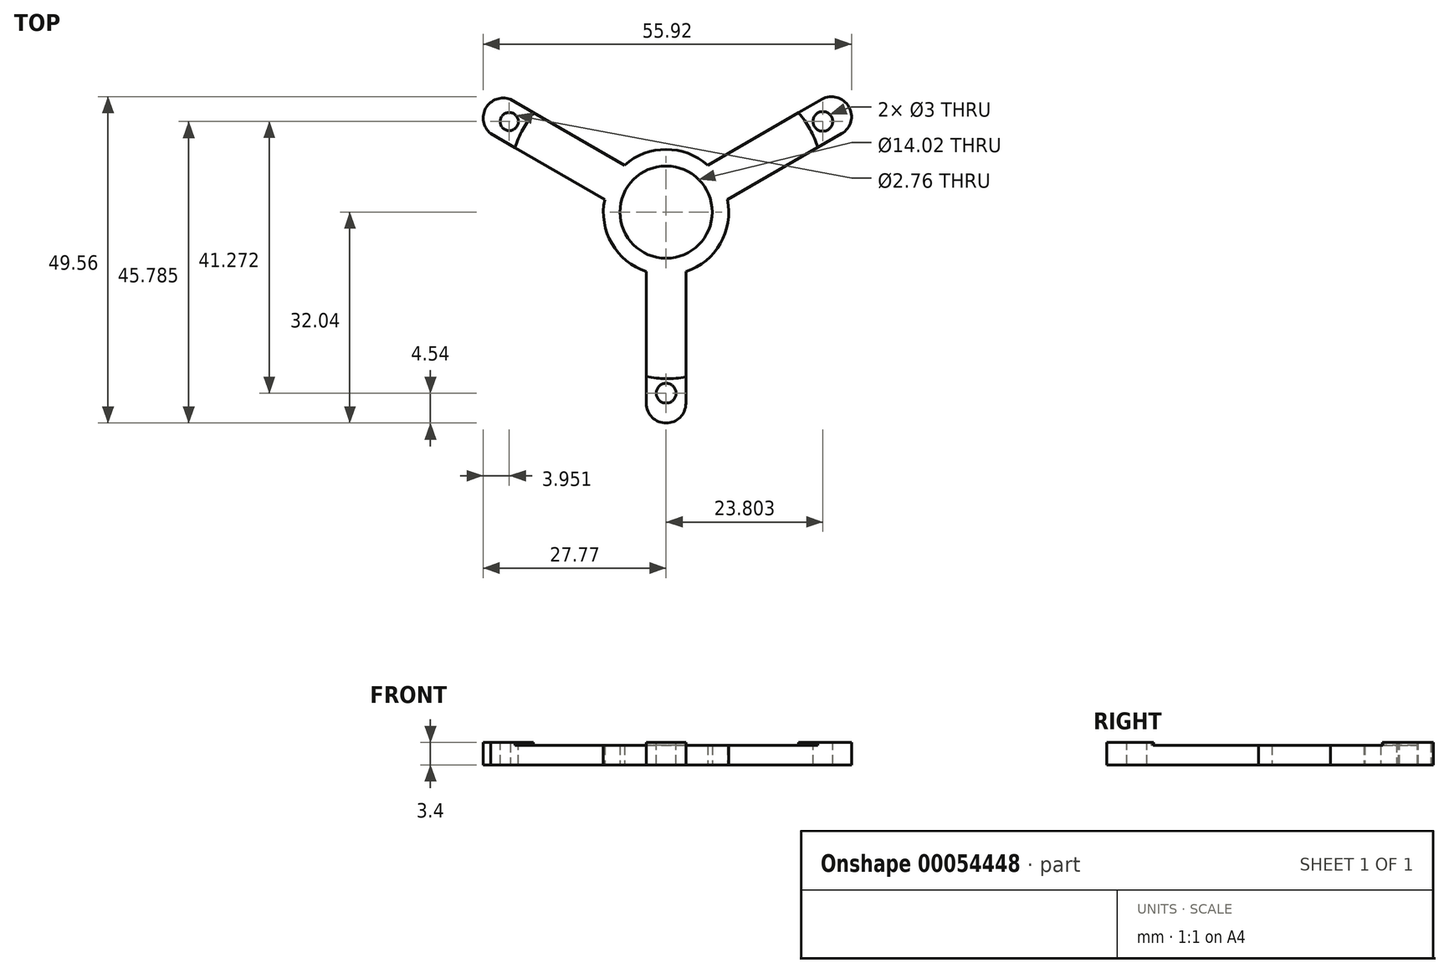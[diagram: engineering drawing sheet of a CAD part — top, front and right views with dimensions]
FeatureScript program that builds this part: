
annotation { "Feature Type Name" : "Feature", "Feature Type Description" : "" }
export const myFeature = defineFeature(function(context is Context, id is Id, definition is map)
    precondition{}
    {
        {
            var Q0;
            Q0=qCreatedBy(makeId("Top.planeOp"),FACE);
            var sketch = newSketch(context, id + "F0", { "sketchPlane" : qUnion([Q0])});
            skCircle(sketch, "E0", {"center": v(0, 0) * mm, "radius": 25.15 * mm, "construction": true});
            skCircle(sketch, "E1", {"center": v(0, 0) * mm, "radius": 30 * mm, "construction": true});
            skLineSegment(sketch, "E2", {"start": v(0, 0) * mm, "end": v(0, -27.5) * mm, "construction": true});
            skLineSegment(sketch, "E3", {"start": v(0, 0) * mm, "end": v(-23.82, 13.75) * mm, "construction": true});
            skLineSegment(sketch, "E4", {"start": v(0, 0) * mm, "end": v(23.82, 13.75) * mm, "construction": true});
            skCircle(sketch, "E5", {"center": v(0, 0) * mm, "radius": 7 * mm, "construction": true});
            skSolve(sketch);
        }
        {
            var Q0;
            Q0=qCreatedBy(makeId("Top.planeOp"),FACE);
            var sketch = newSketch(context, id + "F1", { "sketchPlane" : qUnion([Q0])});
            skCircle(sketch, "E6", {"center": v(0, 0) * mm, "radius": 7 * mm});
            skCircle(sketch, "E7", {"center": v(0, 0) * mm, "radius": 9.52 * mm});
            skLineSegment(sketch, "E8", {"start": v(-6.33, 7.12) * mm, "end": v(-23.65, 17.12) * mm});
            skLineSegment(sketch, "E9", {"start": v(-9.33, 1.92) * mm, "end": v(-26.65, 11.92) * mm});
            skArc(sketch, "E10", {"start": v(-23.65, 17.12) * mm, "mid": v(-27.37, 15.8) * mm, "end": v(-26.65, 11.92) * mm});
            skLineSegment(sketch, "E11", {"start": v(6.33, 7.12) * mm, "end": v(23.65, 17.12) * mm});
            skLineSegment(sketch, "E12", {"start": v(9.33, 1.92) * mm, "end": v(26.65, 11.92) * mm});
            skArc(sketch, "E13", {"start": v(26.65, 11.92) * mm, "mid": v(27.74, 16.02) * mm, "end": v(23.65, 17.12) * mm});
            skLineSegment(sketch, "E14", {"start": v(-3, -9.04) * mm, "end": v(-3, -29.04) * mm});
            skLineSegment(sketch, "E15", {"start": v(3, -9.04) * mm, "end": v(3, -29.04) * mm});
            skArc(sketch, "E16", {"start": v(-3, -29.04) * mm, "mid": v(0, -32.04) * mm, "end": v(3, -29.04) * mm});
            skSolve(sketch);
        }
        {
            var Q0;
            {var subQ0=sQuery(id+"F1.wireOp",EDGE,"E11");Q0=makeQuery(id+"F1.imprint","IMPRINT",FACE,{"disambiguationData":[TD([[makeQuery(id+"F1.imprint","IMPRINT",EDGE,{"derivedFrom":subQ0}),-1.0]])]});}
            var Q1;
            {var subQ0=sQuery(id+"F1.wireOp",EDGE,"E14");Q1=makeQuery(id+"F1.imprint","IMPRINT",FACE,{"disambiguationData":[TD([[makeQuery(id+"F1.imprint","IMPRINT",EDGE,{"derivedFrom":subQ0}),1.0]])]});}
            var Q2;
            Q2=makeQuery(id+"F1.imprint","IMPRINT",FACE,{"disambiguationData":[TD([[makeQuery(id+"F1.imprint","IMPRINT",EDGE,{"derivedFrom":sQuery(id+"F1.wireOp",EDGE,"E6")}),-1.0]])]});
            var Q3;
            {var subQ0=sQuery(id+"F1.wireOp",EDGE,"E8");Q3=makeQuery(id+"F1.imprint","IMPRINT",FACE,{"disambiguationData":[TD([[makeQuery(id+"F1.imprint","IMPRINT",EDGE,{"derivedFrom":subQ0}),1.0]])]});}
            extrude(context, id + "F2", {"entities" : qUnion([Q0, Q1, Q2, Q3]), "depth" : 3 * mm});
        }
        {
            var Q0;
            Q0=makeQuery(id+"F2.opExtrude","CAP_FACE",FACE,{"disambiguationData":[OSD([sQuery(id+"F1.wireOp",EDGE,"E6"),sQuery(id+"F1.wireOp",EDGE,"E7"),sQuery(id+"F1.wireOp",EDGE,"E8"),sQuery(id+"F1.wireOp",EDGE,"E9"),sQuery(id+"F1.wireOp",EDGE,"E10"),sQuery(id+"F1.wireOp",EDGE,"E11"),sQuery(id+"F1.wireOp",EDGE,"E12"),sQuery(id+"F1.wireOp",EDGE,"E13"),sQuery(id+"F1.wireOp",EDGE,"E14"),sQuery(id+"F1.wireOp",EDGE,"E15"),sQuery(id+"F1.wireOp",EDGE,"E16")])],"isStart":false});
            var sketch = newSketch(context, id + "F3", { "sketchPlane" : qUnion([Q0])});
            skCircle(sketch, "E17", {"center": v(-23.82, 13.75) * mm, "radius": 1.38 * mm});
            skCircle(sketch, "E18", {"center": v(23.8, 13.77) * mm, "radius": 1.5 * mm});
            skCircle(sketch, "E19", {"center": v(0, -40.74) * mm, "radius": 1.42 * mm});
            skCircle(sketch, "E20", {"center": v(0, -27.5) * mm, "radius": 1.5 * mm});
            skSolve(sketch);
        }
        {
            var Q0;
            Q0=makeQuery(id+"F3.imprint","IMPRINT",FACE,{"disambiguationData":[TD([[makeQuery(id+"F3.imprint","IMPRINT",EDGE,{"derivedFrom":sQuery(id+"F3.wireOp",EDGE,"E17")}),1.0]])]});
            var Q1;
            {var subQ0=sQuery(id+"F3.wireOp",EDGE,"E18");var subQ1=makeQuery(id+"F2.opExtrude","CAP_EDGE",EDGE,{"disambiguationData":[OSD([sQuery(id+"F1.wireOp",EDGE,"E11")])],"isStart":false});var subQ2=makeQuery(id+"F3.imprint","INTERSECT",VERTEX,{"disambiguationData":[OD(0.0)],"derivedFrom":[subQ1,subQ0]});Q1=makeQuery(id+"F3.imprint","IMPRINT",FACE,{"disambiguationData":[TD([[makeQuery(id+"F3.imprint","IMPRINT",EDGE,{"disambiguationData":[TD([[subQ2,-1.0]])],"derivedFrom":subQ0}),1.0]])]});}
            var Q2;
            {var subQ0=sQuery(id+"F3.wireOp",EDGE,"E20");var subQ1=makeQuery(id+"F3.imprint","INTERSECT",VERTEX,{"derivedFrom":[makeQuery(id+"F2.opExtrude","CAP_EDGE",EDGE,{"disambiguationData":[OSD([sQuery(id+"F1.wireOp",EDGE,"E14")])],"isStart":false}),subQ0]});Q2=makeQuery(id+"F3.imprint","IMPRINT",FACE,{"disambiguationData":[TD([[makeQuery(id+"F3.imprint","IMPRINT",EDGE,{"disambiguationData":[TD([[subQ1,1.0]])],"derivedFrom":subQ0}),1.0]])]});}
            extrude(context, id + "F4", {"entities" : qUnion([Q0, Q1, Q2]), "operationType" : NewBodyOperationType.REMOVE, "oppositeDirection" : true, "depth" : 25 * mm});
        }
        {
            var Q0;
            Q0=makeQuery(id+"F2.opExtrude","CAP_FACE",FACE,{"disambiguationData":[OSD([sQuery(id+"F1.wireOp",EDGE,"E6"),sQuery(id+"F1.wireOp",EDGE,"E7"),sQuery(id+"F1.wireOp",EDGE,"E8"),sQuery(id+"F1.wireOp",EDGE,"E9"),sQuery(id+"F1.wireOp",EDGE,"E10"),sQuery(id+"F1.wireOp",EDGE,"E11"),sQuery(id+"F1.wireOp",EDGE,"E12"),sQuery(id+"F1.wireOp",EDGE,"E13"),sQuery(id+"F1.wireOp",EDGE,"E14"),sQuery(id+"F1.wireOp",EDGE,"E15"),sQuery(id+"F1.wireOp",EDGE,"E16")])],"isStart":false});
            var sketch = newSketch(context, id + "F5", { "sketchPlane" : qUnion([Q0])});
            skArc(sketch, "E21", {"start": v(-20.13, 15.09) * mm, "mid": v(-21.76, 12.55) * mm, "end": v(-22.96, 9.8) * mm});
            skArc(sketch, "E22", {"start": v(23.04, 9.84) * mm, "mid": v(21.84, 12.6) * mm, "end": v(20.12, 15.08) * mm});
            skArc(sketch, "E23", {"start": v(-3, -24.94) * mm, "mid": v(0, -25.3) * mm, "end": v(3, -25.02) * mm});
            skSolve(sketch);
        }
        {
            var Q0;
            {var subQ2=sQuery(id+"F5.wireOp",EDGE,"E21");Q0=makeQuery(id+"F5.imprint","IMPRINT",FACE,{"disambiguationData":[TD([[makeQuery(id+"F5.imprint","IMPRINT",EDGE,{"derivedFrom":subQ2}),-1.0]])]});}
            var Q1;
            {var subQ2=sQuery(id+"F5.wireOp",EDGE,"E22");Q1=makeQuery(id+"F5.imprint","IMPRINT",FACE,{"disambiguationData":[TD([[makeQuery(id+"F5.imprint","IMPRINT",EDGE,{"derivedFrom":subQ2}),-1.0]])]});}
            var Q2;
            {var subQ2=sQuery(id+"F5.wireOp",EDGE,"E23");Q2=makeQuery(id+"F5.imprint","IMPRINT",FACE,{"disambiguationData":[TD([[makeQuery(id+"F5.imprint","IMPRINT",EDGE,{"derivedFrom":subQ2}),-1.0]])]});}
            extrude(context, id + "F6", {"entities" : qUnion([Q0, Q1, Q2]), "operationType" : NewBodyOperationType.ADD, "depth" : .4 * mm});
        }
    });
